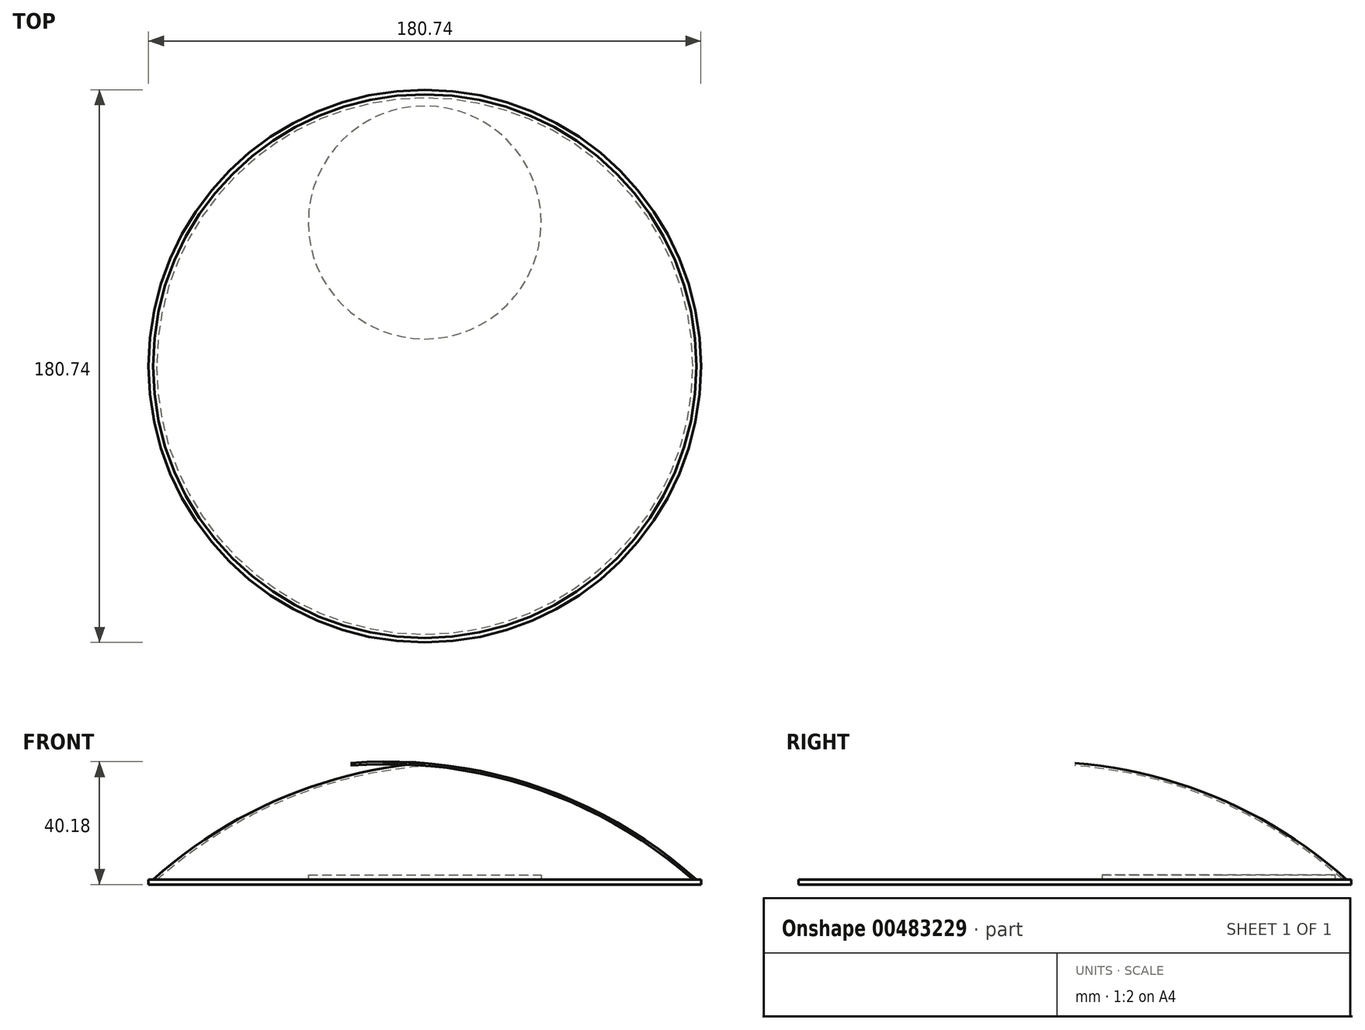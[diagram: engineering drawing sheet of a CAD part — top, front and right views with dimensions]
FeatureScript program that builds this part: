
annotation { "Feature Type Name" : "Feature", "Feature Type Description" : "" }
export const myFeature = defineFeature(function(context is Context, id is Id, definition is map)
    precondition{}
    {
        {
            var Q0;
            Q0=qCreatedBy(makeId("Right.planeOp"),FACE);
            var sketch = newSketch(context, id + "F0", { "sketchPlane" : qUnion([Q0])});
            skLineSegment(sketch, "E0", {"start": v(0, 37.3) * mm, "end": v(0, 38.1) * mm});
            skArc(sketch, "E1", {"start": v(88.9, 0) * mm, "mid": v(47.57, 26.33) * mm, "end": v(0, 38.1) * mm});
            skArc(sketch, "E2.1", {"start": v(87.7, 0) * mm, "mid": v(46.88, 25.77) * mm, "end": v(0, 37.3) * mm});
            skPoint(sketch, "E3.orphan", {"position": v(0, 0) * mm});
            skLineSegment(sketch, "E4", {"start": v(87.7, 0) * mm, "end": v(88.9, 0) * mm});
            skLineSegment(sketch, "E5", {"start": v(0, 0) * mm, "end": v(0, 37.3) * mm, "construction": true});
            skSolve(sketch);
        }
        {
            var Q0;
            Q0 = qSketchRegion(id + "F0", true);
            var Q1;
            Q1=sQuery(id+"F0.wireOp",EDGE,"E5");
            revolve(context, id + "F1", {"entities" : qUnion([Q0]), "axis" : qUnion([Q1]), "revolveType" : RevolveType.FULL});
        }
        {
            var Q0;
            Q0=makeQuery(id+"F1.opRevolve","SWEPT_FACE",FACE,{"disambiguationData":[OSD([sQuery(id+"F0.wireOp",EDGE,"E4")])]});
            var sketch = newSketch(context, id + "F2", { "sketchPlane" : qUnion([Q0])});
            skCircle(sketch, "E6", {"center": v(0, -47) * mm, "radius": 38.1 * mm});
            skSolve(sketch);
        }
        {
            var Q0;
            Q0 = qSketchRegion(id + "F2", true);
            extrude(context, id + "F3", {"entities" : qUnion([Q0]), "oppositeDirection" : true, "depth" : 1.59 * mm});
        }
        {
            var Q0;
            Q0=makeQuery(id+"F3.opExtrude","CAP_FACE",FACE,{"disambiguationData":[OSD([sQuery(id+"F2.wireOp",EDGE,"E6")])],"isStart":true});
            var sketch = newSketch(context, id + "F4", { "sketchPlane" : qUnion([Q0])});
            skCircle(sketch, "E7", {"center": v(0, 0) * mm, "radius": 90.37 * mm});
            skSolve(sketch);
        }
        {
            var Q0;
            Q0 = qSketchRegion(id + "F4", true);
            extrude(context, id + "F5", {"entities" : qUnion([Q0]), "depth" : 1.59 * mm});
        }
    });
